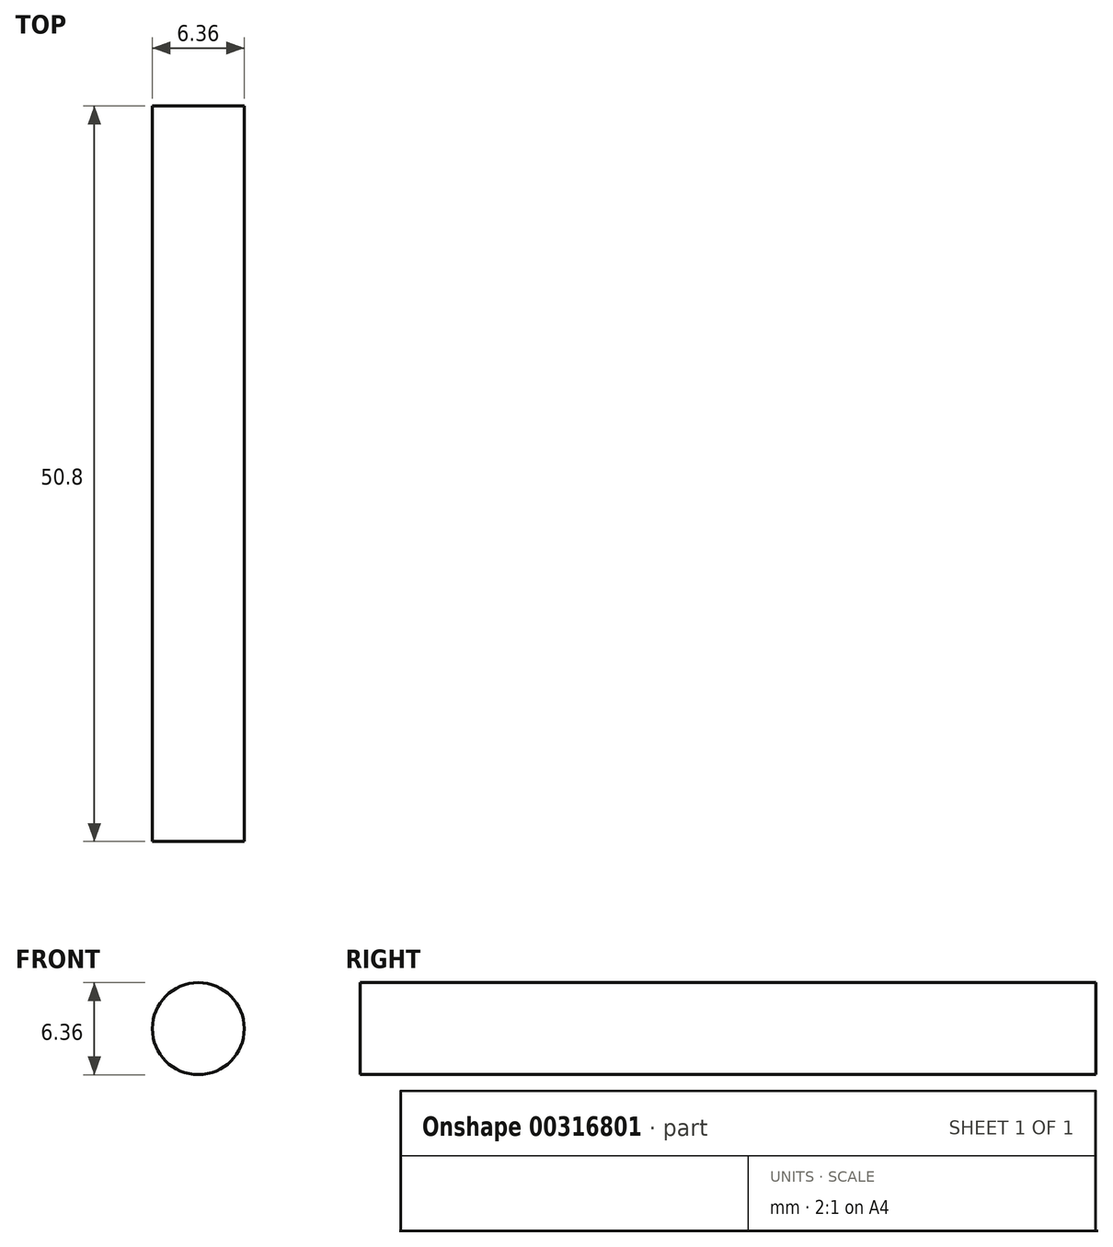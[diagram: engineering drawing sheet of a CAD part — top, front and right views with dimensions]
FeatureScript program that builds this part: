
annotation { "Feature Type Name" : "Feature", "Feature Type Description" : "" }
export const myFeature = defineFeature(function(context is Context, id is Id, definition is map)
    precondition{}
    {
        {
            var Q0;
            Q0=qCreatedBy(makeId("Front.planeOp"),FACE);
            var sketch = newSketch(context, id + "F0", { "sketchPlane" : qUnion([Q0])});
            skCircle(sketch, "E0", {"center": v(0, 0) * mm, "radius": 3.18 * mm});
            skSolve(sketch);
        }
        {
            var Q0;
            Q0=makeQuery(id+"F0.imprint","IMPRINT",FACE,{"disambiguationData":[TD([[makeQuery(id+"F0.imprint","IMPRINT",EDGE,{"derivedFrom":sQuery(id+"F0.wireOp",EDGE,"E0")}),1.0]])]});
            var Q1;
            Q1=sQuery(id+"F0.wireOp",EDGE,"E0");
            extrude(context, id + "F1", {"entities" : qUnion([Q0]), "surfaceEntities" : qUnion([Q1]), "depth" : 50.8 * mm});
        }
    });
